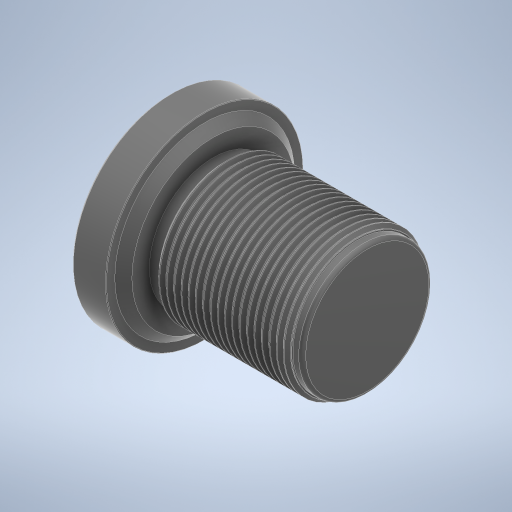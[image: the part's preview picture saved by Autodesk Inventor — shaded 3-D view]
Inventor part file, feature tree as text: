
AUTODESK INVENTOR PART (.ipt)
format: ipt  version: 2024.2 (Build 282272000, 272)  size: 448,000 bytes
history: native  units: mm
features: plane x1
ambient origin geometry x8: Origin, YZ Plane, XZ Plane, XY Plane, X Axis, Y Axis, Z Axis, Center Point
bodies: Solid1 (feature_tree), Solid2 (feature_tree)
feature tree (1):
  plane  "Work Plane1"
